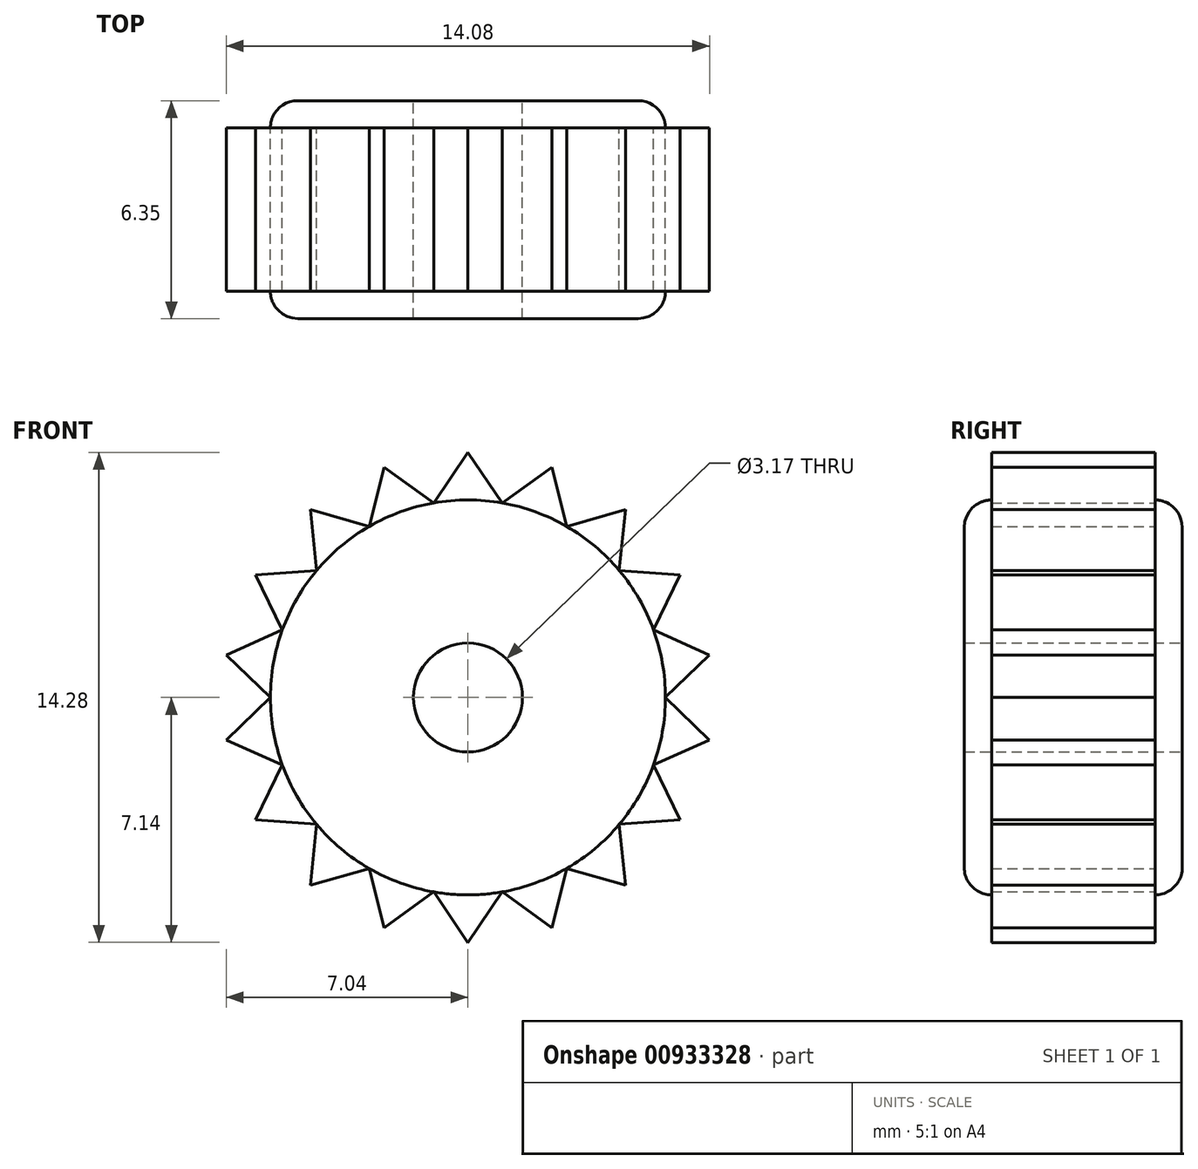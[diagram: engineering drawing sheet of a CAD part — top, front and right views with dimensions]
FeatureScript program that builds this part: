
annotation { "Feature Type Name" : "Feature", "Feature Type Description" : "" }
export const myFeature = defineFeature(function(context is Context, id is Id, definition is map)
    precondition{}
    {
        {
            var Q0;
            Q0=qCreatedBy(makeId("Front.planeOp"),FACE);
            var sketch = newSketch(context, id + "F0", { "sketchPlane" : qUnion([Q0])});
            skCircle(sketch, "E0", {"center": v(0, 0) * mm, "radius": 7.14 * mm});
            skLineSegment(sketch, "E1", {"start": v(0, 13.29) * mm, "end": v(0, -13.03) * mm, "construction": true});
            skLineSegment(sketch, "E2", {"start": v(0, 0) * mm, "end": v(-2.44, 6.71) * mm, "construction": true});
            skLineSegment(sketch, "E3", {"start": v(0, 0) * mm, "end": v(0, 7.14) * mm, "construction": true});
            skLineSegment(sketch, "E4", {"start": v(0, 0) * mm, "end": v(2.44, 6.71) * mm, "construction": true});
            skLineSegment(sketch, "E5", {"start": v(0, 0) * mm, "end": v(4.6, 5.47) * mm, "construction": true});
            skLineSegment(sketch, "E6", {"start": v(0, 0) * mm, "end": v(6.19, 3.57) * mm, "construction": true});
            skLineSegment(sketch, "E7", {"start": v(0, 0) * mm, "end": v(7.04, 1.24) * mm, "construction": true});
            skLineSegment(sketch, "E8", {"start": v(0, 0) * mm, "end": v(7.04, -1.24) * mm, "construction": true});
            skLineSegment(sketch, "E9", {"start": v(0, 0) * mm, "end": v(6.19, -3.57) * mm, "construction": true});
            skLineSegment(sketch, "E10", {"start": v(0, 0) * mm, "end": v(4.6, -5.47) * mm, "construction": true});
            skLineSegment(sketch, "E11", {"start": v(2.44, -6.71) * mm, "end": v(0, 0) * mm, "construction": true});
            skLineSegment(sketch, "E12", {"start": v(0, -7.14) * mm, "end": v(0, 0) * mm, "construction": true});
            skLineSegment(sketch, "E13", {"start": v(-2.44, -6.71) * mm, "end": v(0, 0) * mm, "construction": true});
            skLineSegment(sketch, "E14", {"start": v(-4.6, -5.47) * mm, "end": v(0, 0) * mm, "construction": true});
            skLineSegment(sketch, "E15", {"start": v(-6.19, -3.57) * mm, "end": v(0, 0) * mm, "construction": true});
            skLineSegment(sketch, "E16", {"start": v(-7.04, -1.24) * mm, "end": v(0, 0) * mm, "construction": true});
            skLineSegment(sketch, "E17", {"start": v(-7.04, 1.24) * mm, "end": v(0, 0) * mm, "construction": true});
            skLineSegment(sketch, "E18", {"start": v(-6.19, 3.57) * mm, "end": v(0, 0) * mm, "construction": true});
            skLineSegment(sketch, "E19", {"start": v(-4.6, 5.47) * mm, "end": v(0, 0) * mm, "construction": true});
            skCircle(sketch, "E20", {"center": v(0, 0) * mm, "radius": 5.75 * mm});
            skLineSegment(sketch, "E21", {"start": v(4.6, 5.47) * mm, "end": v(4.4, 3.7) * mm});
            skLineSegment(sketch, "E22", {"start": v(4.4, 3.7) * mm, "end": v(6.19, 3.57) * mm});
            skLineSegment(sketch, "E23", {"start": v(6.19, 3.57) * mm, "end": v(5.4, 1.97) * mm});
            skLineSegment(sketch, "E24", {"start": v(5.4, 1.97) * mm, "end": v(7.04, 1.24) * mm});
            skLineSegment(sketch, "E25", {"start": v(7.04, 1.24) * mm, "end": v(5.75, 0) * mm});
            skLineSegment(sketch, "E26", {"start": v(5.75, 0) * mm, "end": v(7.04, -1.24) * mm});
            skLineSegment(sketch, "E27", {"start": v(7.04, -1.24) * mm, "end": v(5.4, -1.97) * mm});
            skLineSegment(sketch, "E28", {"start": v(5.4, -1.97) * mm, "end": v(6.19, -3.57) * mm});
            skLineSegment(sketch, "E29", {"start": v(6.19, -3.57) * mm, "end": v(4.4, -3.7) * mm});
            skLineSegment(sketch, "E30", {"start": v(4.4, -3.7) * mm, "end": v(4.6, -5.47) * mm});
            skLineSegment(sketch, "E31", {"start": v(4.6, -5.47) * mm, "end": v(2.88, -4.98) * mm});
            skLineSegment(sketch, "E32", {"start": v(2.88, -4.98) * mm, "end": v(2.44, -6.71) * mm});
            skLineSegment(sketch, "E33", {"start": v(2.44, -6.71) * mm, "end": v(1, -5.67) * mm});
            skLineSegment(sketch, "E34", {"start": v(1, -5.67) * mm, "end": v(0, -7.14) * mm});
            skLineSegment(sketch, "E35", {"start": v(0, -7.14) * mm, "end": v(-1, -5.67) * mm});
            skLineSegment(sketch, "E36", {"start": v(-1, -5.67) * mm, "end": v(-2.44, -6.71) * mm});
            skLineSegment(sketch, "E37", {"start": v(-2.44, -6.71) * mm, "end": v(-2.88, -4.98) * mm});
            skLineSegment(sketch, "E38", {"start": v(-2.88, -4.98) * mm, "end": v(-4.6, -5.47) * mm});
            skLineSegment(sketch, "E39", {"start": v(-4.6, -5.47) * mm, "end": v(-4.4, -3.7) * mm});
            skLineSegment(sketch, "E40", {"start": v(-4.4, -3.7) * mm, "end": v(-6.19, -3.57) * mm});
            skLineSegment(sketch, "E41", {"start": v(-6.19, -3.57) * mm, "end": v(-5.4, -1.97) * mm});
            skLineSegment(sketch, "E42", {"start": v(-5.4, -1.97) * mm, "end": v(-7.04, -1.24) * mm});
            skLineSegment(sketch, "E43", {"start": v(-7.04, -1.24) * mm, "end": v(-5.75, 0) * mm});
            skLineSegment(sketch, "E44", {"start": v(-5.75, 0) * mm, "end": v(-7.04, 1.24) * mm});
            skLineSegment(sketch, "E45", {"start": v(-7.04, 1.24) * mm, "end": v(-5.4, 1.97) * mm});
            skLineSegment(sketch, "E46", {"start": v(-5.4, 1.97) * mm, "end": v(-6.19, 3.57) * mm});
            skLineSegment(sketch, "E47", {"start": v(-6.19, 3.57) * mm, "end": v(-4.4, 3.7) * mm});
            skLineSegment(sketch, "E48", {"start": v(-4.4, 3.7) * mm, "end": v(-4.6, 5.47) * mm});
            skLineSegment(sketch, "E49", {"start": v(-4.6, 5.47) * mm, "end": v(-2.88, 4.98) * mm});
            skLineSegment(sketch, "E50", {"start": v(-2.88, 4.98) * mm, "end": v(-2.44, 6.71) * mm});
            skLineSegment(sketch, "E51", {"start": v(-2.44, 6.71) * mm, "end": v(-1, 5.67) * mm});
            skLineSegment(sketch, "E52", {"start": v(-1, 5.67) * mm, "end": v(0, 7.14) * mm});
            skLineSegment(sketch, "E53", {"start": v(0, 7.14) * mm, "end": v(1, 5.67) * mm});
            skLineSegment(sketch, "E54", {"start": v(1, 5.67) * mm, "end": v(2.44, 6.71) * mm});
            skLineSegment(sketch, "E55", {"start": v(2.44, 6.71) * mm, "end": v(2.88, 4.98) * mm});
            skLineSegment(sketch, "E56", {"start": v(2.88, 4.98) * mm, "end": v(4.6, 5.47) * mm});
            skLineSegment(sketch, "E57", {"start": v(-2.88, 4.98) * mm, "end": v(0, 0) * mm, "construction": true});
            skLineSegment(sketch, "E58", {"start": v(-1, 5.67) * mm, "end": v(0, 0) * mm, "construction": true});
            skLineSegment(sketch, "E59", {"start": v(1, 5.67) * mm, "end": v(0, 0) * mm, "construction": true});
            skLineSegment(sketch, "E60", {"start": v(2.88, 4.98) * mm, "end": v(0, 0) * mm, "construction": true});
            skLineSegment(sketch, "E61", {"start": v(4.4, 3.7) * mm, "end": v(0, 0) * mm, "construction": true});
            skLineSegment(sketch, "E62", {"start": v(5.4, 1.97) * mm, "end": v(0, 0) * mm, "construction": true});
            skLineSegment(sketch, "E63", {"start": v(5.75, 0) * mm, "end": v(0, 0) * mm, "construction": true});
            skLineSegment(sketch, "E64", {"start": v(5.4, -1.97) * mm, "end": v(0, 0) * mm, "construction": true});
            skLineSegment(sketch, "E65", {"start": v(4.4, -3.7) * mm, "end": v(0, 0) * mm, "construction": true});
            skLineSegment(sketch, "E66", {"start": v(2.88, -4.98) * mm, "end": v(0, 0) * mm, "construction": true});
            skLineSegment(sketch, "E67", {"start": v(1, -5.67) * mm, "end": v(0, 0) * mm, "construction": true});
            skLineSegment(sketch, "E68", {"start": v(-1, -5.67) * mm, "end": v(0, 0) * mm, "construction": true});
            skLineSegment(sketch, "E69", {"start": v(-2.88, -4.98) * mm, "end": v(0, 0) * mm, "construction": true});
            skLineSegment(sketch, "E70", {"start": v(-4.4, -3.7) * mm, "end": v(0, 0) * mm, "construction": true});
            skLineSegment(sketch, "E71", {"start": v(-5.4, -1.97) * mm, "end": v(0, 0) * mm, "construction": true});
            skLineSegment(sketch, "E72", {"start": v(-5.75, 0) * mm, "end": v(0, 0) * mm, "construction": true});
            skLineSegment(sketch, "E73", {"start": v(-5.4, 1.97) * mm, "end": v(0, 0) * mm, "construction": true});
            skLineSegment(sketch, "E74", {"start": v(-4.4, 3.7) * mm, "end": v(0, 0) * mm, "construction": true});
            skCircle(sketch, "E75", {"center": v(0, 0) * mm, "radius": 1.59 * mm});
            skSolve(sketch);
        }
        {
            var Q0;
            Q0=makeQuery(id+"F0.imprint","IMPRINT",FACE,{"disambiguationData":[TD([[makeQuery(id+"F0.imprint","IMPRINT",EDGE,{"derivedFrom":sQuery(id+"F0.wireOp",EDGE,"E21")}),-1.0]])]});
            extrude(context, id + "F1", {"entities" : qUnion([Q0]), "depth" : 4.76 * mm, "offsetDistance" : 25.4 * mm});
        }
        {
            var Q0;
            {var subQ0=sQuery(id+"F0.wireOp",EDGE,"E36");Q0=makeQuery(id+"F0.imprint","IMPRINT",FACE,{"disambiguationData":[TD([[makeQuery(id+"F0.imprint","IMPRINT",EDGE,{"derivedFrom":subQ0}),-1.0]])]});}
            var Q1;
            {var subQ0=sQuery(id+"F0.wireOp",EDGE,"E32");Q1=makeQuery(id+"F0.imprint","IMPRINT",FACE,{"disambiguationData":[TD([[makeQuery(id+"F0.imprint","IMPRINT",EDGE,{"derivedFrom":subQ0}),-1.0]])]});}
            var Q2;
            {var subQ0=sQuery(id+"F0.wireOp",EDGE,"E44");Q2=makeQuery(id+"F0.imprint","IMPRINT",FACE,{"disambiguationData":[TD([[makeQuery(id+"F0.imprint","IMPRINT",EDGE,{"derivedFrom":subQ0}),-1.0]])]});}
            var Q3;
            {var subQ0=sQuery(id+"F0.wireOp",EDGE,"E34");Q3=makeQuery(id+"F0.imprint","IMPRINT",FACE,{"disambiguationData":[TD([[makeQuery(id+"F0.imprint","IMPRINT",EDGE,{"derivedFrom":subQ0}),-1.0]])]});}
            var Q4;
            {var subQ0=sQuery(id+"F0.wireOp",EDGE,"E52");Q4=makeQuery(id+"F0.imprint","IMPRINT",FACE,{"disambiguationData":[TD([[makeQuery(id+"F0.imprint","IMPRINT",EDGE,{"derivedFrom":subQ0}),-1.0]])]});}
            var Q5;
            {var subQ0=sQuery(id+"F0.wireOp",EDGE,"E40");Q5=makeQuery(id+"F0.imprint","IMPRINT",FACE,{"disambiguationData":[TD([[makeQuery(id+"F0.imprint","IMPRINT",EDGE,{"derivedFrom":subQ0}),-1.0]])]});}
            var Q6;
            {var subQ0=sQuery(id+"F0.wireOp",EDGE,"E28");Q6=makeQuery(id+"F0.imprint","IMPRINT",FACE,{"disambiguationData":[TD([[makeQuery(id+"F0.imprint","IMPRINT",EDGE,{"derivedFrom":subQ0}),-1.0]])]});}
            var Q7;
            {var subQ0=sQuery(id+"F0.wireOp",EDGE,"E38");Q7=makeQuery(id+"F0.imprint","IMPRINT",FACE,{"disambiguationData":[TD([[makeQuery(id+"F0.imprint","IMPRINT",EDGE,{"derivedFrom":subQ0}),-1.0]])]});}
            var Q8;
            {var subQ0=sQuery(id+"F0.wireOp",EDGE,"E30");Q8=makeQuery(id+"F0.imprint","IMPRINT",FACE,{"disambiguationData":[TD([[makeQuery(id+"F0.imprint","IMPRINT",EDGE,{"derivedFrom":subQ0}),-1.0]])]});}
            var Q9;
            {var subQ0=sQuery(id+"F0.wireOp",EDGE,"E22");Q9=makeQuery(id+"F0.imprint","IMPRINT",FACE,{"disambiguationData":[TD([[makeQuery(id+"F0.imprint","IMPRINT",EDGE,{"derivedFrom":subQ0}),-1.0]])]});}
            var Q10;
            {var subQ0=sQuery(id+"F0.wireOp",EDGE,"E50");Q10=makeQuery(id+"F0.imprint","IMPRINT",FACE,{"disambiguationData":[TD([[makeQuery(id+"F0.imprint","IMPRINT",EDGE,{"derivedFrom":subQ0}),-1.0]])]});}
            var Q11;
            {var subQ0=sQuery(id+"F0.wireOp",EDGE,"E42");Q11=makeQuery(id+"F0.imprint","IMPRINT",FACE,{"disambiguationData":[TD([[makeQuery(id+"F0.imprint","IMPRINT",EDGE,{"derivedFrom":subQ0}),-1.0]])]});}
            var Q12;
            Q12=makeQuery(id+"F0.imprint","IMPRINT",FACE,{"disambiguationData":[TD([[makeQuery(id+"F0.imprint","IMPRINT",EDGE,{"derivedFrom":sQuery(id+"F0.wireOp",EDGE,"E75")}),-1.0]])]});
            var Q13;
            {var subQ0=sQuery(id+"F0.wireOp",EDGE,"E24");Q13=makeQuery(id+"F0.imprint","IMPRINT",FACE,{"disambiguationData":[TD([[makeQuery(id+"F0.imprint","IMPRINT",EDGE,{"derivedFrom":subQ0}),-1.0]])]});}
            var Q14;
            {var subQ0=sQuery(id+"F0.wireOp",EDGE,"E26");Q14=makeQuery(id+"F0.imprint","IMPRINT",FACE,{"disambiguationData":[TD([[makeQuery(id+"F0.imprint","IMPRINT",EDGE,{"derivedFrom":subQ0}),-1.0]])]});}
            var Q15;
            {var subQ0=sQuery(id+"F0.wireOp",EDGE,"E21");Q15=makeQuery(id+"F0.imprint","IMPRINT",FACE,{"disambiguationData":[TD([[makeQuery(id+"F0.imprint","IMPRINT",EDGE,{"derivedFrom":subQ0}),-1.0]])]});}
            var Q16;
            {var subQ0=sQuery(id+"F0.wireOp",EDGE,"E48");Q16=makeQuery(id+"F0.imprint","IMPRINT",FACE,{"disambiguationData":[TD([[makeQuery(id+"F0.imprint","IMPRINT",EDGE,{"derivedFrom":subQ0}),-1.0]])]});}
            var Q17;
            {var subQ0=sQuery(id+"F0.wireOp",EDGE,"E46");Q17=makeQuery(id+"F0.imprint","IMPRINT",FACE,{"disambiguationData":[TD([[makeQuery(id+"F0.imprint","IMPRINT",EDGE,{"derivedFrom":subQ0}),-1.0]])]});}
            var Q18;
            {var subQ0=sQuery(id+"F0.wireOp",EDGE,"E54");Q18=makeQuery(id+"F0.imprint","IMPRINT",FACE,{"disambiguationData":[TD([[makeQuery(id+"F0.imprint","IMPRINT",EDGE,{"derivedFrom":subQ0}),-1.0]])]});}
            extrude(context, id + "F2", {"entities" : qUnion([Q0, Q1, Q2, Q3, Q4, Q5, Q6, Q7, Q8, Q9, Q10, Q11, Q12, Q13, Q14, Q15, Q16, Q17, Q18]), "operationType" : NewBodyOperationType.ADD, "depth" : 4.76 * mm, "offsetDistance" : 25.4 * mm});
        }
        {
            var Q0;
            Q0=makeQuery(id+"F0.imprint","IMPRINT",FACE,{"disambiguationData":[TD([[makeQuery(id+"F0.imprint","IMPRINT",EDGE,{"derivedFrom":sQuery(id+"F0.wireOp",EDGE,"E75")}),-1.0]])]});
            extrude(context, id + "F3", {"entities" : qUnion([Q0]), "operationType" : NewBodyOperationType.ADD, "depth" : 5.56 * mm, "offsetDistance" : 25.4 * mm});
        }
        {
            var Q0;
            Q0=makeQuery(id+"F0.imprint","IMPRINT",FACE,{"disambiguationData":[TD([[makeQuery(id+"F0.imprint","IMPRINT",EDGE,{"derivedFrom":sQuery(id+"F0.wireOp",EDGE,"E75")}),-1.0]])]});
            extrude(context, id + "F4", {"entities" : qUnion([Q0]), "operationType" : NewBodyOperationType.ADD, "oppositeDirection" : true, "depth" : 0.8 * mm, "offsetDistance" : 25.4 * mm});
        }
        {
            var Q0;
            Q0=makeQuery(id+"F4.opExtrude","CAP_EDGE",EDGE,{"disambiguationData":[OSD([sQuery(id+"F0.wireOp",EDGE,"E20")])],"isStart":false});
            var Q1;
            Q1=makeQuery(id+"F3.opExtrude","CAP_EDGE",EDGE,{"disambiguationData":[OSD([sQuery(id+"F0.wireOp",EDGE,"E20")])],"isStart":false});
            fillet(context, id + "F5", {"entities" : qUnion([Q0, Q1]), "radius" : 0.8 * mm, "tangentPropagation" : true, "allowEdgeOverflow" : false});
        }
    });
